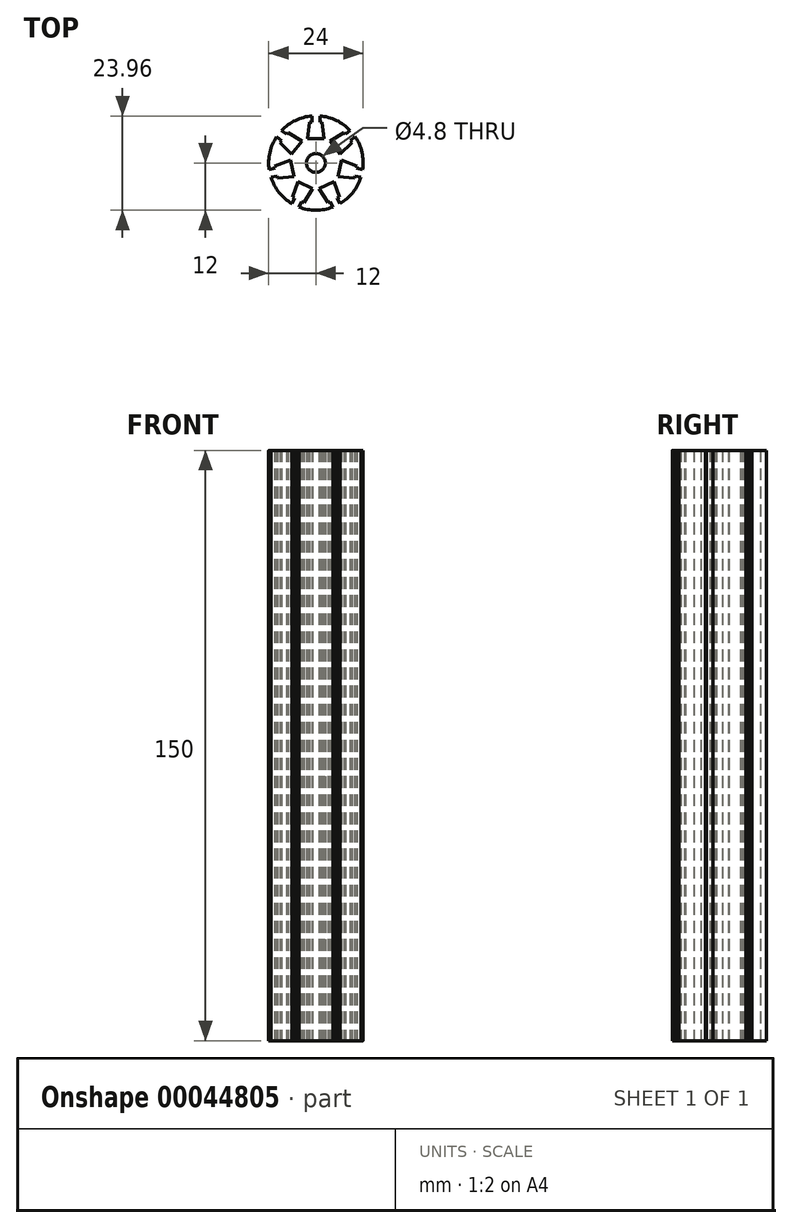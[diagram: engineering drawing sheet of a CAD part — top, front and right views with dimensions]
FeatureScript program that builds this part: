
annotation { "Feature Type Name" : "Feature", "Feature Type Description" : "" }
export const myFeature = defineFeature(function(context is Context, id is Id, definition is map)
    precondition{}
    {
        {
            var Q0;
            Q0=qCreatedBy(makeId("Top.planeOp"),FACE);
            var sketch = newSketch(context, id + "F0", { "sketchPlane" : qUnion([Q0])});
            skCircle(sketch, "E0", {"center": v(0, 0) * mm, "radius": 12 * mm});
            skLineSegment(sketch, "E1", {"start": v(0, 12) * mm, "end": v(0, -12) * mm, "construction": true});
            skCircle(sketch, "E2", {"center": v(0, 0) * mm, "radius": 2.4 * mm});
            skLineSegment(sketch, "E3.rect.bottom", {"start": v(1, 12) * mm, "end": v(-1, 12) * mm});
            skLineSegment(sketch, "E3.rect.top", {"start": v(1, 10.4) * mm, "end": v(-1, 10.4) * mm});
            skLineSegment(sketch, "E3.rect.left", {"start": v(1, 12) * mm, "end": v(1, 10.4) * mm});
            skLineSegment(sketch, "E3.rect.right", {"start": v(-1, 12) * mm, "end": v(-1, 10.4) * mm});
            skPoint(sketch, "E3.rect.middle", {"position": v(0, 11.2) * mm});
            skLineSegment(sketch, "E4.rect.bottom", {"start": v(2.1, 10.4) * mm, "end": v(-2.1, 10.4) * mm, "construction": true});
            skLineSegment(sketch, "E4.rect.top", {"start": v(2.1, 6.2) * mm, "end": v(-2.1, 6.2) * mm});
            skLineSegment(sketch, "E4.rect.left", {"start": v(2.1, 10.4) * mm, "end": v(2.1, 6.2) * mm, "construction": true});
            skLineSegment(sketch, "E4.rect.right", {"start": v(-2.1, 10.4) * mm, "end": v(-2.1, 6.2) * mm, "construction": true});
            skPoint(sketch, "E4.rect.middle", {"position": v(0, 8.3) * mm});
            skLineSegment(sketch, "E5", {"start": v(-1.6, 10.4) * mm, "end": v(1.6, 10.4) * mm});
            skPoint(sketch, "E6", {"position": v(0, 10.4) * mm});
            skLineSegment(sketch, "E7", {"start": v(-1.6, 10.4) * mm, "end": v(-2.1, 6.2) * mm});
            skLineSegment(sketch, "E8", {"start": v(1.6, 10.4) * mm, "end": v(2.1, 6.2) * mm});
            skPoint(sketch, "E9.1.0", {"position": v(-8.76, 6.98) * mm});
            skPoint(sketch, "E9.1.1", {"position": v(-8.13, 6.48) * mm});
            skLineSegment(sketch, "E9.1.2", {"start": v(-8.76, 8.26) * mm, "end": v(-7.5, 7.27) * mm});
            skLineSegment(sketch, "E9.1.3", {"start": v(-9.44, 4.84) * mm, "end": v(-6.16, 2.22) * mm, "construction": true});
            skPoint(sketch, "E9.1.4", {"position": v(-6.49, 5.17) * mm});
            skLineSegment(sketch, "E9.1.5", {"start": v(-10, 6.7) * mm, "end": v(-8.75, 5.7) * mm});
            skLineSegment(sketch, "E9.1.6", {"start": v(-7.13, 7.74) * mm, "end": v(-3.54, 5.5) * mm});
            skLineSegment(sketch, "E9.1.7", {"start": v(-9.13, 5.23) * mm, "end": v(-6.16, 2.22) * mm});
            skLineSegment(sketch, "E9.1.8", {"start": v(-3.54, 5.5) * mm, "end": v(-6.16, 2.22) * mm});
            skLineSegment(sketch, "E9.1.9", {"start": v(-6.82, 8.13) * mm, "end": v(-3.54, 5.5) * mm, "construction": true});
            skLineSegment(sketch, "E9.1.10", {"start": v(-9.13, 5.23) * mm, "end": v(-7.13, 7.74) * mm});
            skLineSegment(sketch, "E9.1.11", {"start": v(-8.76, 8.26) * mm, "end": v(-10, 6.7) * mm});
            skLineSegment(sketch, "E9.1.12", {"start": v(-7.5, 7.27) * mm, "end": v(-8.75, 5.7) * mm});
            skLineSegment(sketch, "E9.1.13", {"start": v(-6.82, 8.13) * mm, "end": v(-9.44, 4.84) * mm, "construction": true});
            skPoint(sketch, "E9.2.0", {"position": v(-10.92, -2.5) * mm});
            skPoint(sketch, "E9.2.1", {"position": v(-10.14, -2.31) * mm});
            skLineSegment(sketch, "E9.2.2", {"start": v(-11.92, -1.7) * mm, "end": v(-10.36, -1.34) * mm});
            skLineSegment(sketch, "E9.2.3", {"start": v(-9.67, -4.36) * mm, "end": v(-5.58, -3.43) * mm, "construction": true});
            skPoint(sketch, "E9.2.4", {"position": v(-8.1, -1.85) * mm});
            skLineSegment(sketch, "E9.2.5", {"start": v(-11.48, -3.65) * mm, "end": v(-9.92, -3.29) * mm});
            skLineSegment(sketch, "E9.2.6", {"start": v(-10.5, -0.75) * mm, "end": v(-6.51, 0.67) * mm});
            skLineSegment(sketch, "E9.2.7", {"start": v(-9.78, -3.87) * mm, "end": v(-5.58, -3.43) * mm});
            skLineSegment(sketch, "E9.2.8", {"start": v(-6.51, 0.67) * mm, "end": v(-5.58, -3.43) * mm});
            skLineSegment(sketch, "E9.2.9", {"start": v(-10.6, -0.27) * mm, "end": v(-6.51, 0.67) * mm, "construction": true});
            skLineSegment(sketch, "E9.2.10", {"start": v(-9.78, -3.87) * mm, "end": v(-10.5, -0.75) * mm});
            skLineSegment(sketch, "E9.2.11", {"start": v(-11.92, -1.7) * mm, "end": v(-11.48, -3.65) * mm});
            skLineSegment(sketch, "E9.2.12", {"start": v(-10.36, -1.34) * mm, "end": v(-9.92, -3.29) * mm});
            skLineSegment(sketch, "E9.2.13", {"start": v(-10.6, -0.27) * mm, "end": v(-9.67, -4.36) * mm, "construction": true});
            skPoint(sketch, "E10.0.3.0", {"position": v(-4.86, -10.1) * mm});
            skPoint(sketch, "E10.1.3.0", {"position": v(-4.51, -9.37) * mm});
            skLineSegment(sketch, "E10.2.3.0", {"start": v(-6.1, -10.38) * mm, "end": v(-5.41, -8.94) * mm});
            skLineSegment(sketch, "E10.5.3.0", {"start": v(-2.62, -10.28) * mm, "end": v(-0.8, -6.5) * mm, "construction": true});
            skPoint(sketch, "E10.8.3.0", {"position": v(-3.6, -7.48) * mm});
            skLineSegment(sketch, "E10.9.3.0", {"start": v(-4.3, -11.25) * mm, "end": v(-3.61, -9.8) * mm});
            skLineSegment(sketch, "E10.12.3.0", {"start": v(-5.95, -8.68) * mm, "end": v(-4.58, -4.67) * mm});
            skLineSegment(sketch, "E10.15.3.0", {"start": v(-3.07, -10.06) * mm, "end": v(-0.8, -6.5) * mm});
            skLineSegment(sketch, "E10.18.3.0", {"start": v(-4.58, -4.67) * mm, "end": v(-0.8, -6.5) * mm});
            skLineSegment(sketch, "E10.21.3.0", {"start": v(-6.4, -8.46) * mm, "end": v(-4.58, -4.67) * mm, "construction": true});
            skLineSegment(sketch, "E10.24.3.0", {"start": v(-3.07, -10.06) * mm, "end": v(-5.95, -8.68) * mm});
            skLineSegment(sketch, "E10.27.3.0", {"start": v(-6.1, -10.38) * mm, "end": v(-4.3, -11.25) * mm});
            skLineSegment(sketch, "E10.30.3.0", {"start": v(-5.41, -8.94) * mm, "end": v(-3.61, -9.8) * mm});
            skLineSegment(sketch, "E10.33.3.0", {"start": v(-6.4, -8.46) * mm, "end": v(-2.62, -10.28) * mm, "construction": true});
            skPoint(sketch, "E10.0.4.0", {"position": v(4.86, -10.1) * mm});
            skPoint(sketch, "E10.1.4.0", {"position": v(4.51, -9.37) * mm});
            skLineSegment(sketch, "E10.2.4.0", {"start": v(4.3, -11.25) * mm, "end": v(3.61, -9.8) * mm});
            skLineSegment(sketch, "E10.5.4.0", {"start": v(6.4, -8.46) * mm, "end": v(4.58, -4.67) * mm, "construction": true});
            skPoint(sketch, "E10.8.4.0", {"position": v(3.6, -7.48) * mm});
            skLineSegment(sketch, "E10.9.4.0", {"start": v(6.1, -10.38) * mm, "end": v(5.41, -8.94) * mm});
            skLineSegment(sketch, "E10.12.4.0", {"start": v(3.07, -10.06) * mm, "end": v(0.8, -6.5) * mm});
            skLineSegment(sketch, "E10.15.4.0", {"start": v(5.95, -8.68) * mm, "end": v(4.58, -4.67) * mm});
            skLineSegment(sketch, "E10.18.4.0", {"start": v(0.8, -6.5) * mm, "end": v(4.58, -4.67) * mm});
            skLineSegment(sketch, "E10.21.4.0", {"start": v(2.62, -10.28) * mm, "end": v(0.8, -6.5) * mm, "construction": true});
            skLineSegment(sketch, "E10.24.4.0", {"start": v(5.95, -8.68) * mm, "end": v(3.07, -10.06) * mm});
            skLineSegment(sketch, "E10.27.4.0", {"start": v(4.3, -11.25) * mm, "end": v(6.1, -10.38) * mm});
            skLineSegment(sketch, "E10.30.4.0", {"start": v(3.61, -9.8) * mm, "end": v(5.41, -8.94) * mm});
            skLineSegment(sketch, "E10.33.4.0", {"start": v(2.62, -10.28) * mm, "end": v(6.4, -8.46) * mm, "construction": true});
            skPoint(sketch, "E10.0.5.0", {"position": v(10.92, -2.5) * mm});
            skPoint(sketch, "E10.1.5.0", {"position": v(10.14, -2.31) * mm});
            skLineSegment(sketch, "E10.2.5.0", {"start": v(11.48, -3.65) * mm, "end": v(9.92, -3.29) * mm});
            skLineSegment(sketch, "E10.5.5.0", {"start": v(10.6, -0.27) * mm, "end": v(6.51, 0.67) * mm, "construction": true});
            skPoint(sketch, "E10.8.5.0", {"position": v(8.1, -1.85) * mm});
            skLineSegment(sketch, "E10.9.5.0", {"start": v(11.92, -1.7) * mm, "end": v(10.36, -1.34) * mm});
            skLineSegment(sketch, "E10.12.5.0", {"start": v(9.78, -3.87) * mm, "end": v(5.58, -3.43) * mm});
            skLineSegment(sketch, "E10.15.5.0", {"start": v(10.5, -0.75) * mm, "end": v(6.51, 0.67) * mm});
            skLineSegment(sketch, "E10.18.5.0", {"start": v(5.58, -3.43) * mm, "end": v(6.51, 0.67) * mm});
            skLineSegment(sketch, "E10.21.5.0", {"start": v(9.67, -4.36) * mm, "end": v(5.58, -3.43) * mm, "construction": true});
            skLineSegment(sketch, "E10.24.5.0", {"start": v(10.5, -0.75) * mm, "end": v(9.78, -3.87) * mm});
            skLineSegment(sketch, "E10.27.5.0", {"start": v(11.48, -3.65) * mm, "end": v(11.92, -1.7) * mm});
            skLineSegment(sketch, "E10.30.5.0", {"start": v(9.92, -3.29) * mm, "end": v(10.36, -1.34) * mm});
            skLineSegment(sketch, "E10.33.5.0", {"start": v(9.67, -4.36) * mm, "end": v(10.6, -0.27) * mm, "construction": true});
            skPoint(sketch, "E10.0.6.0", {"position": v(8.76, 6.98) * mm});
            skPoint(sketch, "E10.1.6.0", {"position": v(8.13, 6.48) * mm});
            skLineSegment(sketch, "E10.2.6.0", {"start": v(10, 6.7) * mm, "end": v(8.75, 5.7) * mm});
            skLineSegment(sketch, "E10.5.6.0", {"start": v(6.82, 8.13) * mm, "end": v(3.54, 5.5) * mm, "construction": true});
            skPoint(sketch, "E10.8.6.0", {"position": v(6.49, 5.17) * mm});
            skLineSegment(sketch, "E10.9.6.0", {"start": v(8.76, 8.26) * mm, "end": v(7.5, 7.27) * mm});
            skLineSegment(sketch, "E10.12.6.0", {"start": v(9.13, 5.23) * mm, "end": v(6.16, 2.22) * mm});
            skLineSegment(sketch, "E10.15.6.0", {"start": v(7.13, 7.74) * mm, "end": v(3.54, 5.5) * mm});
            skLineSegment(sketch, "E10.18.6.0", {"start": v(6.16, 2.22) * mm, "end": v(3.54, 5.5) * mm});
            skLineSegment(sketch, "E10.21.6.0", {"start": v(9.44, 4.84) * mm, "end": v(6.16, 2.22) * mm, "construction": true});
            skLineSegment(sketch, "E10.24.6.0", {"start": v(7.13, 7.74) * mm, "end": v(9.13, 5.23) * mm});
            skLineSegment(sketch, "E10.27.6.0", {"start": v(10, 6.7) * mm, "end": v(8.76, 8.26) * mm});
            skLineSegment(sketch, "E10.30.6.0", {"start": v(8.75, 5.7) * mm, "end": v(7.5, 7.27) * mm});
            skLineSegment(sketch, "E10.33.6.0", {"start": v(9.44, 4.84) * mm, "end": v(6.82, 8.13) * mm, "construction": true});
            skSolve(sketch);
        }
        {
            var Q0;
            {var subQ1=sQuery(id+"F0.wireOp",EDGE,"ea57cd78-9a61-45f1-bd1d-7b98c58c8d17.7.3");Q0=makeQuery(id+"F0.imprint","IMPRINT",FACE,{"disambiguationData":[TD([[makeQuery(id+"F0.imprint","IMPRINT",EDGE,{"derivedFrom":subQ1}),1.0]])]});}
            var Q1;
            {var subQ2=sQuery(id+"F0.wireOp",EDGE,"ea57cd78-9a61-45f1-bd1d-7b98c58c8d17.7.2");Q1=makeQuery(id+"F0.imprint","IMPRINT",FACE,{"disambiguationData":[TD([[makeQuery(id+"F0.imprint","IMPRINT",EDGE,{"derivedFrom":subQ2}),1.0]])]});}
            var Q2;
            {var subQ1=sQuery(id+"F0.wireOp",EDGE,"ea57cd78-9a61-45f1-bd1d-7b98c58c8d17.1.3");Q2=makeQuery(id+"F0.imprint","IMPRINT",FACE,{"disambiguationData":[TD([[makeQuery(id+"F0.imprint","IMPRINT",EDGE,{"derivedFrom":subQ1}),1.0]])]});}
            var Q3;
            {var subQ2=sQuery(id+"F0.wireOp",EDGE,"ea57cd78-9a61-45f1-bd1d-7b98c58c8d17.1.2");Q3=makeQuery(id+"F0.imprint","IMPRINT",FACE,{"disambiguationData":[TD([[makeQuery(id+"F0.imprint","IMPRINT",EDGE,{"derivedFrom":subQ2}),1.0]])]});}
            var Q4;
            {var subQ1=sQuery(id+"F0.wireOp",EDGE,"ea57cd78-9a61-45f1-bd1d-7b98c58c8d17.2.3");Q4=makeQuery(id+"F0.imprint","IMPRINT",FACE,{"disambiguationData":[TD([[makeQuery(id+"F0.imprint","IMPRINT",EDGE,{"derivedFrom":subQ1}),1.0]])]});}
            var Q5;
            {var subQ2=sQuery(id+"F0.wireOp",EDGE,"ea57cd78-9a61-45f1-bd1d-7b98c58c8d17.2.2");Q5=makeQuery(id+"F0.imprint","IMPRINT",FACE,{"disambiguationData":[TD([[makeQuery(id+"F0.imprint","IMPRINT",EDGE,{"derivedFrom":subQ2}),1.0]])]});}
            var Q6;
            {var subQ1=sQuery(id+"F0.wireOp",EDGE,"ea57cd78-9a61-45f1-bd1d-7b98c58c8d17.3.3");Q6=makeQuery(id+"F0.imprint","IMPRINT",FACE,{"disambiguationData":[TD([[makeQuery(id+"F0.imprint","IMPRINT",EDGE,{"derivedFrom":subQ1}),1.0]])]});}
            var Q7;
            {var subQ2=sQuery(id+"F0.wireOp",EDGE,"ea57cd78-9a61-45f1-bd1d-7b98c58c8d17.3.2");Q7=makeQuery(id+"F0.imprint","IMPRINT",FACE,{"disambiguationData":[TD([[makeQuery(id+"F0.imprint","IMPRINT",EDGE,{"derivedFrom":subQ2}),1.0]])]});}
            var Q8;
            {var subQ1=sQuery(id+"F0.wireOp",EDGE,"ea57cd78-9a61-45f1-bd1d-7b98c58c8d17.4.3");Q8=makeQuery(id+"F0.imprint","IMPRINT",FACE,{"disambiguationData":[TD([[makeQuery(id+"F0.imprint","IMPRINT",EDGE,{"derivedFrom":subQ1}),1.0]])]});}
            var Q9;
            {var subQ2=sQuery(id+"F0.wireOp",EDGE,"ea57cd78-9a61-45f1-bd1d-7b98c58c8d17.4.2");Q9=makeQuery(id+"F0.imprint","IMPRINT",FACE,{"disambiguationData":[TD([[makeQuery(id+"F0.imprint","IMPRINT",EDGE,{"derivedFrom":subQ2}),1.0]])]});}
            var Q10;
            {var subQ1=sQuery(id+"F0.wireOp",EDGE,"ea57cd78-9a61-45f1-bd1d-7b98c58c8d17.5.3");Q10=makeQuery(id+"F0.imprint","IMPRINT",FACE,{"disambiguationData":[TD([[makeQuery(id+"F0.imprint","IMPRINT",EDGE,{"derivedFrom":subQ1}),1.0]])]});}
            var Q11;
            Q11=makeQuery(id+"F0.imprint","IMPRINT",FACE,{"disambiguationData":[TD([[makeQuery(id+"F0.imprint","IMPRINT",EDGE,{"derivedFrom":sQuery(id+"F0.wireOp",EDGE,"E2")}),-1.0]])]});
            var Q12;
            {var subQ2=sQuery(id+"F0.wireOp",EDGE,"ea57cd78-9a61-45f1-bd1d-7b98c58c8d17.6.2");Q12=makeQuery(id+"F0.imprint","IMPRINT",FACE,{"disambiguationData":[TD([[makeQuery(id+"F0.imprint","IMPRINT",EDGE,{"derivedFrom":subQ2}),1.0]])]});}
            var Q13;
            {var subQ1=sQuery(id+"F0.wireOp",EDGE,"ea57cd78-9a61-45f1-bd1d-7b98c58c8d17.6.3");Q13=makeQuery(id+"F0.imprint","IMPRINT",FACE,{"disambiguationData":[TD([[makeQuery(id+"F0.imprint","IMPRINT",EDGE,{"derivedFrom":subQ1}),1.0]])]});}
            var Q14;
            {var subQ2=sQuery(id+"F0.wireOp",EDGE,"ea57cd78-9a61-45f1-bd1d-7b98c58c8d17.5.2");Q14=makeQuery(id+"F0.imprint","IMPRINT",FACE,{"disambiguationData":[TD([[makeQuery(id+"F0.imprint","IMPRINT",EDGE,{"derivedFrom":subQ2}),1.0]])]});}
            extrude(context, id + "F1", {"entities" : qUnion([Q0, Q1, Q2, Q3, Q4, Q5, Q6, Q7, Q8, Q9, Q10, Q11, Q12, Q13, Q14]), "depth" : 150 * mm});
        }
    });
